# Revit family: P2229_Wing_Shape_Fitting
name_source: partatom
category: Generic Models
units: mm (PartAtom-declared; Revit-internal decimal feet)

## family parameters
Always vertical = No
Can host rebar = No
Cut with Voids When Loaded = No
OmniClass Number = 23.80.30.17.17
OmniClass Title = Cable Trays and Horizontal Racks
Part Type = Normal
Room Calculation Point = No
Round Connector Dimension = Use Diameter
Shared = No
Work Plane-Based = Yes

## types (5) — shared parameters
Center Distance From Top = 0.809 "
Default Elevation = 48 "
Depth = 1.625 "
Description = P2229 - Wing Shape Fitting
Disclaimer = https://www.unistrut.us
Hole Diameter = 0.563 "
Manufacturer = Atkore Unistrut
Model = P2229
Salsify ID1 = US-P2229
Thickness = 0.25 "
Type Comments = 80_77_27_15
URL = https://www.atkore.com
Width = 1.656 "
Wing Length = 3.75 "

## per-type parameters (varying)
| type | Center Distance From Edge | Material | Power-Strut Part Number | UPC | Weight |
| P2229 EG | 0.813 " | Electro Galvanized | PS 669 EG | "78636402728" | 2.3 lbm |
| P2229 HG | 0.828 " | Hot Dip Galvanized |  | "786364027302" | 2.44 lbm |
| P2229 GR | 0.813 " | Green |  | "786364027296" | 2.3 lbm |
| P2229 SS | 0.813 " | Stainless Steel |  | "786364050287" | 2.3 lbm |
| P2229 ZD | 0.828 " | Zinc Dichromate |  | "786364040172" | 2.3 lbm |

note: column(s) folded — value = type name in every type: Part Number

## geometry (parser evidence)
native form markers: Sweep x2
no freeform markers — native parametric forms only
